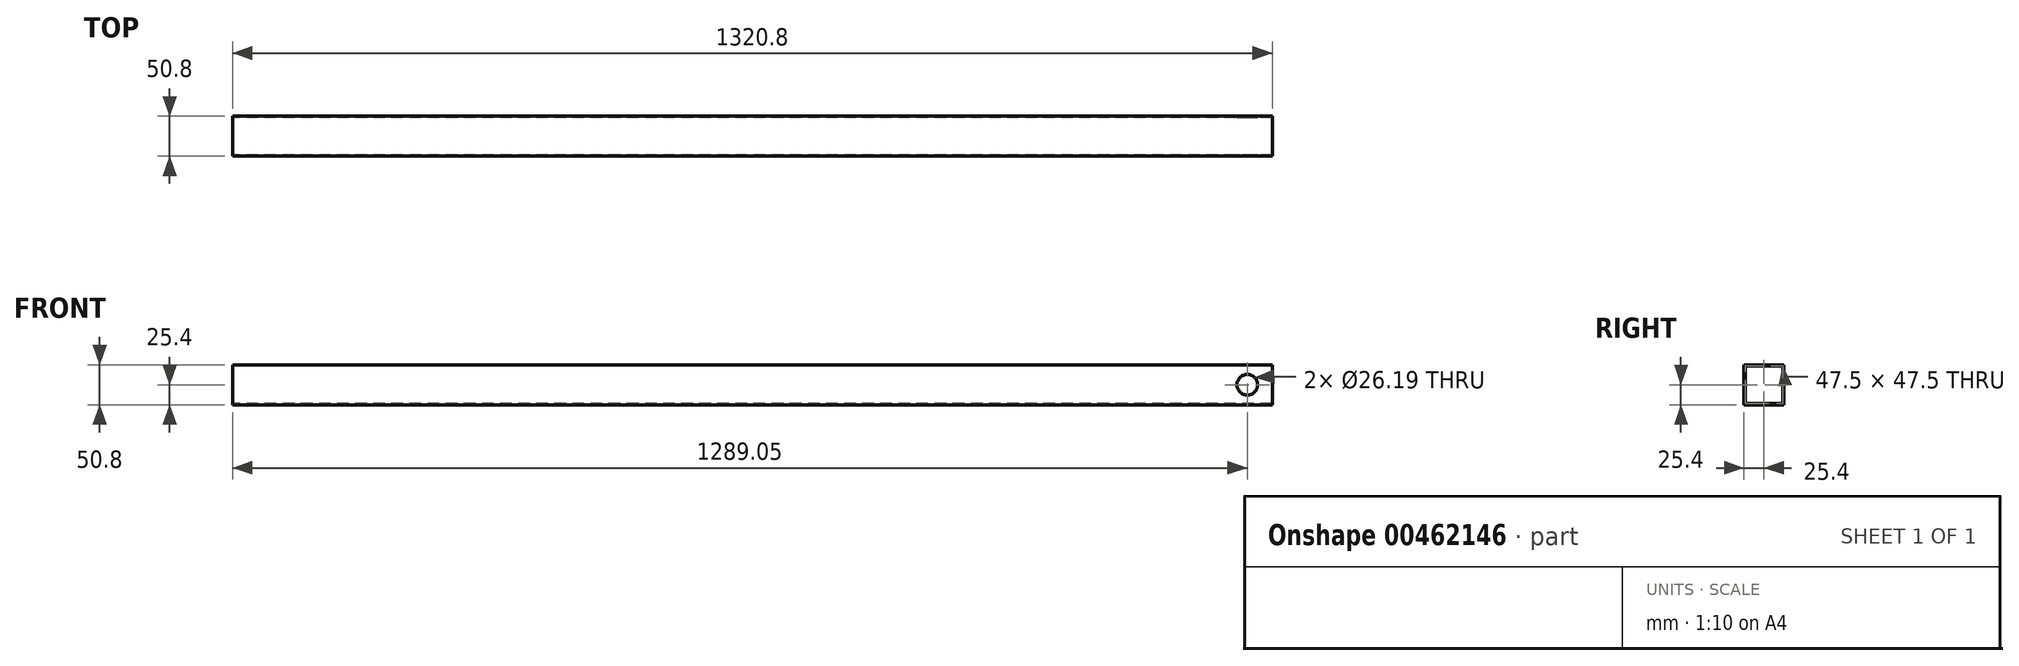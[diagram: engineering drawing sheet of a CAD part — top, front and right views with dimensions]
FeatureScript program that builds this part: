
annotation { "Feature Type Name" : "Feature", "Feature Type Description" : "" }
export const myFeature = defineFeature(function(context is Context, id is Id, definition is map)
    precondition{}
    {
        {
            var Q0;
            Q0=qCreatedBy(makeId("Right.planeOp"),FACE);
            var sketch = newSketch(context, id + "F0", { "sketchPlane" : qUnion([Q0])});
            skLineSegment(sketch, "E0.bottom", {"start": v(0, 0) * mm, "end": v(50.8, 0) * mm});
            skLineSegment(sketch, "E0.top", {"start": v(0, 50.8) * mm, "end": v(50.8, 50.8) * mm});
            skLineSegment(sketch, "E0.left", {"start": v(0, 0) * mm, "end": v(0, 50.8) * mm});
            skLineSegment(sketch, "E0.right", {"start": v(50.8, 0) * mm, "end": v(50.8, 50.8) * mm});
            skLineSegment(sketch, "E1.0", {"start": v(1.65, 49.15) * mm, "end": v(49.15, 49.15) * mm});
            skLineSegment(sketch, "E1.1", {"start": v(1.65, 1.65) * mm, "end": v(1.65, 49.15) * mm});
            skLineSegment(sketch, "E1.2", {"start": v(1.65, 1.65) * mm, "end": v(49.15, 1.65) * mm});
            skLineSegment(sketch, "E1.3", {"start": v(49.15, 1.65) * mm, "end": v(49.15, 49.15) * mm});
            skSolve(sketch);
        }
        {
            var Q0;
            Q0 = qSketchRegion(id + "F0", true);
            extrude(context, id + "F1", {"entities" : qUnion([Q0]), "depth" : 1320.8 * mm});
        }
        {
            var Q0;
            Q0=makeQuery(id+"F1.opExtrude","SWEPT_FACE",FACE,{"disambiguationData":[OSD([sQuery(id+"F0.wireOp",EDGE,"E0.left")])]});
            var sketch = newSketch(context, id + "F2", { "sketchPlane" : qUnion([Q0])});
            skLineSegment(sketch, "E2", {"start": v(1320.8, 25.4) * mm, "end": v(1074.61, 25.4) * mm, "construction": true});
            skCircle(sketch, "E3", {"center": v(1289.05, 25.4) * mm, "radius": 13.1 * mm});
            skSolve(sketch);
        }
        {
            var Q0;
            Q0 = qSketchRegion(id + "F2", true);
            extrude(context, id + "F3", {"entities" : qUnion([Q0]), "operationType" : NewBodyOperationType.REMOVE, "endBound" : BoundingType.THROUGH_ALL, "oppositeDirection" : true, "depth" : 25.4 * mm});
        }
    });
